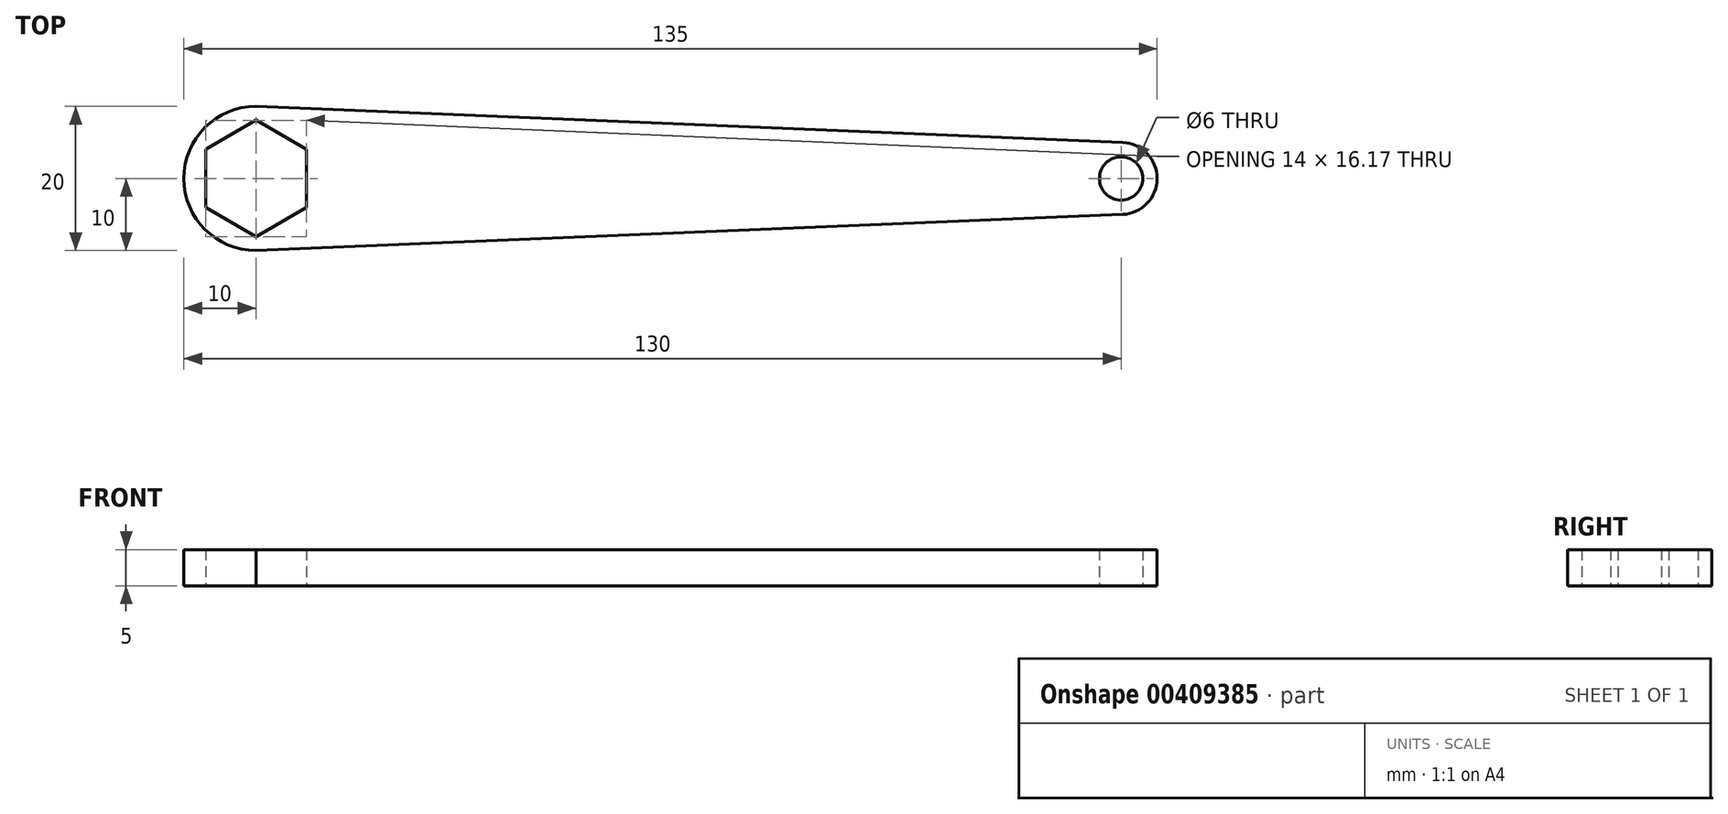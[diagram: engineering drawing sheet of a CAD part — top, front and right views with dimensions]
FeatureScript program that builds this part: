
annotation { "Feature Type Name" : "Feature", "Feature Type Description" : "" }
export const myFeature = defineFeature(function(context is Context, id is Id, definition is map)
    precondition{}
    {
        {
            var Q0;
            Q0=qCreatedBy(makeId("Top.planeOp"),FACE);
            var sketch = newSketch(context, id + "F0", { "sketchPlane" : qUnion([Q0])});
            skCircle(sketch, "E0.cCircle", {"center": v(0, 0) * mm, "radius": 7 * mm, "construction": true});
            skLineSegment(sketch, "E0.0", {"start": v(7, 4.04) * mm, "end": v(7, -4.04) * mm});
            skLineSegment(sketch, "E0.1", {"start": v(7, -4.04) * mm, "end": v(0, -8.08) * mm});
            skLineSegment(sketch, "E0.2", {"start": v(0, -8.08) * mm, "end": v(-7, -4.04) * mm});
            skLineSegment(sketch, "E0.3", {"start": v(-7, -4.04) * mm, "end": v(-7, 4.04) * mm});
            skLineSegment(sketch, "E0.4", {"start": v(-7, 4.04) * mm, "end": v(0, 8.08) * mm});
            skLineSegment(sketch, "E0.5", {"start": v(0, 8.08) * mm, "end": v(7, 4.04) * mm});
            skPoint(sketch, "E0.0.midPoint", {"position": v(7, 0) * mm});
            skArc(sketch, "E1", {"start": v(0.83, 9.97) * mm, "mid": v(-10, 0) * mm, "end": v(0.83, -9.97) * mm});
            skArc(sketch, "E2", {"start": v(120.2, -5) * mm, "mid": v(125, 0) * mm, "end": v(120.2, 5) * mm});
            skCircle(sketch, "E3", {"center": v(120, 0) * mm, "radius": 3 * mm});
            skLineSegment(sketch, "E4", {"start": v(0, 10) * mm, "end": v(120.2, 5) * mm});
            skLineSegment(sketch, "E5", {"start": v(0, -10) * mm, "end": v(120.2, -5) * mm});
            skSolve(sketch);
        }
        {
            var Q0;
            Q0=makeQuery(id+"F0.imprint","IMPRINT",FACE,{"disambiguationData":[TD([[makeQuery(id+"F0.imprint","IMPRINT",EDGE,{"derivedFrom":sQuery(id+"F0.wireOp",EDGE,"E0.0")}),1.0]])]});
            extrude(context, id + "F1", {"entities" : qUnion([Q0]), "depth" : 5 * mm});
        }
    });
